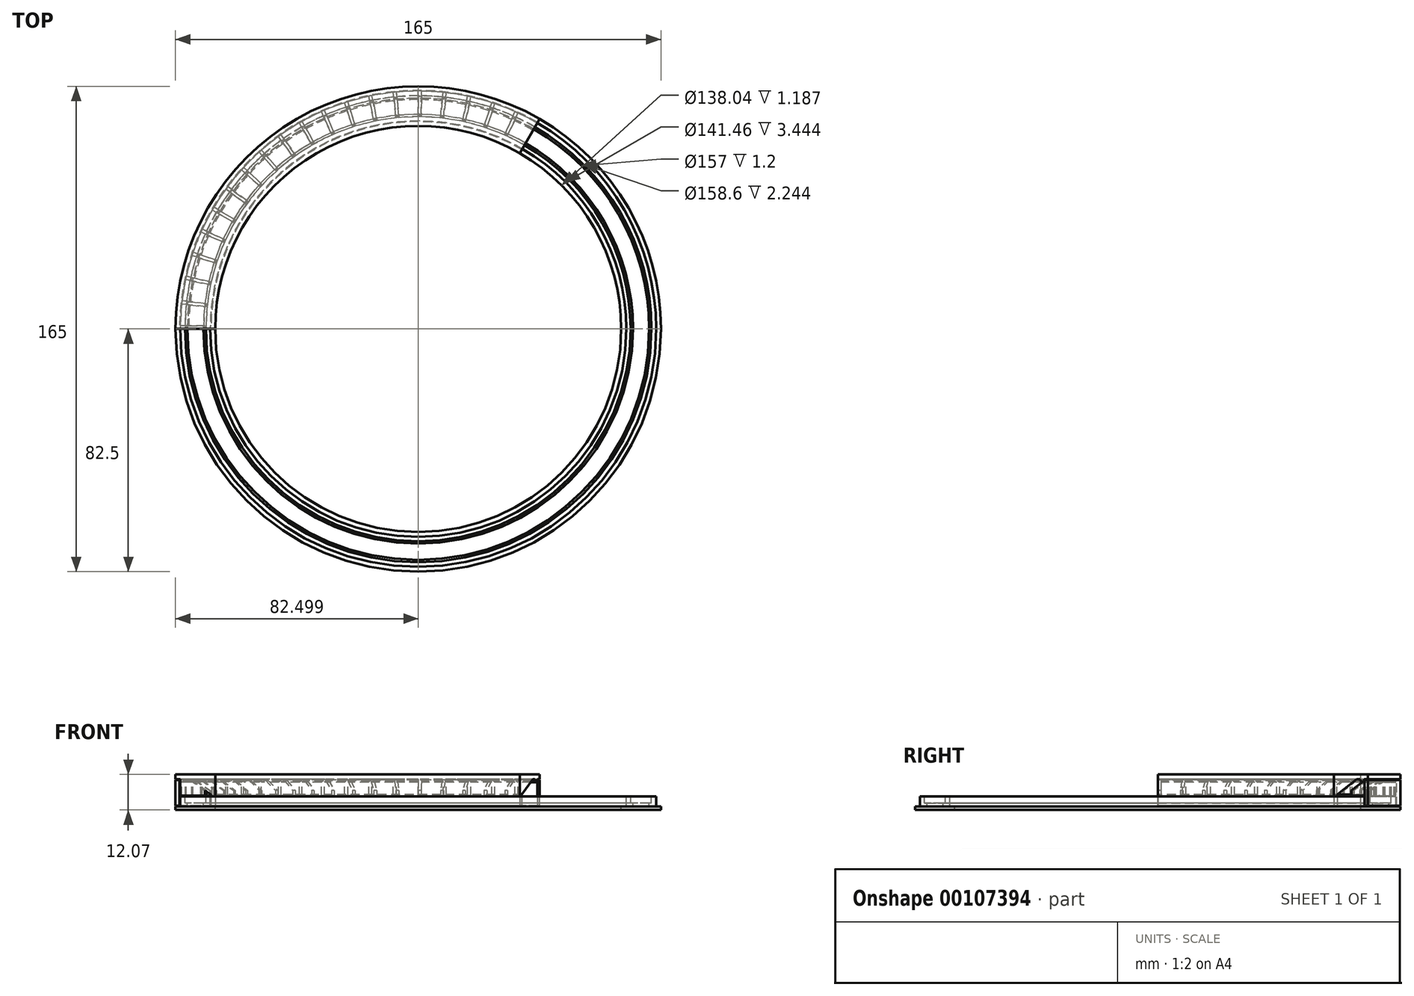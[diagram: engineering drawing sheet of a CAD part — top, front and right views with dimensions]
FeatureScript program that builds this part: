
annotation { "Feature Type Name" : "Feature", "Feature Type Description" : "" }
export const myFeature = defineFeature(function(context is Context, id is Id, definition is map)
    precondition{}
    {
        {
            var Q0;
            Q0=qCreatedBy(makeId("Front.planeOp"),FACE);
            var sketch = newSketch(context, id + "F0", { "sketchPlane" : qUnion([Q0])});
            skLineSegment(sketch, "E0", {"start": v(-1.98, -7.22) * mm, "end": v(4.52, -7.22) * mm, "construction": true});
            skLineSegment(sketch, "E1", {"start": v(-1.98, -7.22) * mm, "end": v(-1.98, -5.52) * mm, "construction": true});
            skLineSegment(sketch, "E2", {"start": v(-1.98, -5.52) * mm, "end": v(4.52, -5.52) * mm, "construction": true});
            skLineSegment(sketch, "E3", {"start": v(4.52, -5.52) * mm, "end": v(4.52, -7.22) * mm, "construction": true});
            skLineSegment(sketch, "E4", {"start": v(-0.98, -5.52) * mm, "end": v(-0.98, -3.92) * mm, "construction": true});
            skLineSegment(sketch, "E5", {"start": v(-0.98, -3.92) * mm, "end": v(3.52, -3.92) * mm, "construction": true});
            skLineSegment(sketch, "E6", {"start": v(3.52, -3.92) * mm, "end": v(3.52, -5.52) * mm, "construction": true});
            skLineSegment(sketch, "E7", {"start": v(-2.28, -8.42) * mm, "end": v(6.3, -8.42) * mm, "construction": true});
            skLineSegment(sketch, "E8", {"start": v(6.54, -4.4) * mm, "end": v(-2.28, 1.78) * mm});
            skLineSegment(sketch, "E9", {"start": v(3.52, -3.92) * mm, "end": v(3.52, -2.28) * mm, "construction": true});
            skLineSegment(sketch, "E10", {"start": v(3.52, -2.28) * mm, "end": v(-15.6, -9.24) * mm, "construction": true});
            skLineSegment(sketch, "E11", {"start": v(6.3, -8.42) * mm, "end": v(-13.34, -8.42) * mm, "construction": true});
            skLineSegment(sketch, "E12", {"start": v(8, -8.42) * mm, "end": v(6.3, -8.42) * mm});
            skLineSegment(sketch, "E13", {"start": v(-0.98, -3.92) * mm, "end": v(-0.98, 0.87) * mm, "construction": true});
            skLineSegment(sketch, "E14", {"start": v(-0.98, 0.87) * mm, "end": v(-10.79, -2.7) * mm, "construction": true});
            skLineSegment(sketch, "E15", {"start": v(-2.28, -8.42) * mm, "end": v(-3.88, -8.42) * mm});
            skLineSegment(sketch, "E16", {"start": v(-3.88, -8.42) * mm, "end": v(-3.88, -4.97) * mm});
            skLineSegment(sketch, "E17", {"start": v(-3.88, -4.97) * mm, "end": v(-2.28, -4.97) * mm});
            skLineSegment(sketch, "E18", {"start": v(-2.28, -4.97) * mm, "end": v(-2.28, -8.42) * mm});
            skLineSegment(sketch, "E19", {"start": v(-0.98, 0.87) * mm, "end": v(-3.88, 0.87) * mm});
            skLineSegment(sketch, "E20", {"start": v(-3.88, 0.87) * mm, "end": v(-3.88, 2.47) * mm});
            skLineSegment(sketch, "E21", {"start": v(-3.88, 2.47) * mm, "end": v(8, 2.47) * mm});
            skLineSegment(sketch, "E22", {"start": v(4.02, -7.22) * mm, "end": v(4.02, -8.42) * mm});
            skLineSegment(sketch, "E23", {"start": v(4.02, -8.42) * mm, "end": v(6.3, -8.42) * mm});
            skLineSegment(sketch, "E24", {"start": v(-3.88, -8.42) * mm, "end": v(-3.88, -9.6) * mm});
            skLineSegment(sketch, "E25", {"start": v(-3.88, -9.6) * mm, "end": v(6.3, -9.6) * mm});
            skLineSegment(sketch, "E26", {"start": v(6.3, -9.6) * mm, "end": v(6.3, -8.42) * mm});
            skLineSegment(sketch, "E27", {"start": v(4.02, -8.42) * mm, "end": v(-2.28, -8.42) * mm});
            skLineSegment(sketch, "E28", {"start": v(8, -8.42) * mm, "end": v(8, -9.6) * mm});
            skLineSegment(sketch, "E29", {"start": v(8, -9.6) * mm, "end": v(6.3, -9.6) * mm});
            skLineSegment(sketch, "E30", {"start": v(-2.28, -7.22) * mm, "end": v(-1.48, -7.22) * mm});
            skLineSegment(sketch, "E31", {"start": v(-1.48, -7.22) * mm, "end": v(-1.48, -8.42) * mm});
            skLineSegment(sketch, "E32", {"start": v(77.02, 5.77) * mm, "end": v(77.02, -11.17) * mm, "construction": true});
            skLineSegment(sketch, "E33", {"start": v(-3.88, -8.42) * mm, "end": v(-5.48, -8.42) * mm});
            skLineSegment(sketch, "E34", {"start": v(-5.48, -8.42) * mm, "end": v(-5.48, -9.6) * mm});
            skLineSegment(sketch, "E35", {"start": v(-5.48, -9.6) * mm, "end": v(-3.88, -9.6) * mm});
            skLineSegment(sketch, "E36", {"start": v(-2.28, 0.87) * mm, "end": v(-2.28, 0.41) * mm});
            skLineSegment(sketch, "E37", {"start": v(-3.88, -0.18) * mm, "end": v(-3.88, 0.87) * mm});
            skLineSegment(sketch, "E38", {"start": v(-3.88, 2.47) * mm, "end": v(-5.48, 2.47) * mm});
            skLineSegment(sketch, "E39", {"start": v(-5.48, 2.47) * mm, "end": v(-5.48, 0.87) * mm});
            skLineSegment(sketch, "E40", {"start": v(-5.48, 0.87) * mm, "end": v(-3.88, 0.87) * mm});
            skLineSegment(sketch, "E41", {"start": v(-5.48, 0.62) * mm, "end": v(-4.13, 0.62) * mm});
            skLineSegment(sketch, "E42", {"start": v(-4.13, 0.62) * mm, "end": v(-4.13, -8.17) * mm});
            skLineSegment(sketch, "E43", {"start": v(-4.13, -8.17) * mm, "end": v(-5.48, -8.17) * mm});
            skLineSegment(sketch, "E44", {"start": v(-5.48, -8.17) * mm, "end": v(-5.48, 0.62) * mm});
            skLineSegment(sketch, "E45", {"start": v(6.3, -5.13) * mm, "end": v(6.3, -8.42) * mm});
            skLineSegment(sketch, "E46", {"start": v(4.02, -7.22) * mm, "end": v(4.82, -7.22) * mm});
            skLineSegment(sketch, "E47", {"start": v(4.52, -4.12) * mm, "end": v(4.52, 2.47) * mm});
            skLineSegment(sketch, "E48", {"start": v(-2.28, 0.41) * mm, "end": v(-3.88, -0.18) * mm});
            skLineSegment(sketch, "E49", {"start": v(-3.88, -4.12) * mm, "end": v(-3.88, -0.18) * mm});
            skLineSegment(sketch, "E50", {"start": v(4.52, -4.12) * mm, "end": v(4.52, -4.72) * mm});
            skPoint(sketch, "E50.endSnap0", {"position": v(3.52, -4.72) * mm});
            skLineSegment(sketch, "E51", {"start": v(4.52, -4.72) * mm, "end": v(-1.98, -4.72) * mm});
            skLineSegment(sketch, "E52", {"start": v(-3.88, -4.72) * mm, "end": v(-3.88, -4.12) * mm});
            skLineSegment(sketch, "E53", {"start": v(-1.98, -4.72) * mm, "end": v(-1.98, -4.72) * mm});
            skLineSegment(sketch, "E54", {"start": v(-1.98, -4.72) * mm, "end": v(-3.88, -4.72) * mm});
            skLineSegment(sketch, "E55", {"start": v(-3.88, -4.72) * mm, "end": v(-3.88, -4.72) * mm});
            skLineSegment(sketch, "E56", {"start": v(4.82, -4.97) * mm, "end": v(4.82, -8.42) * mm});
            skLineSegment(sketch, "E57", {"start": v(4.82, -4.97) * mm, "end": v(6.3, -4.97) * mm});
            skLineSegment(sketch, "E58", {"start": v(6.3, -4.97) * mm, "end": v(6.3, -5.13) * mm});
            skLineSegment(sketch, "E59", {"start": v(4.52, -4.72) * mm, "end": v(6.54, -4.72) * mm});
            skLineSegment(sketch, "E60", {"start": v(6.54, -8.17) * mm, "end": v(8, -8.17) * mm});
            skLineSegment(sketch, "E61", {"start": v(6.54, -4.4) * mm, "end": v(6.54, -8.17) * mm});
            skLineSegment(sketch, "E62", {"start": v(8, 2.47) * mm, "end": v(8, -8.17) * mm});
            skSolve(sketch);
        }
        {
            var Q0;
            Q0=makeQuery(id+"F0.imprint","IMPRINT",FACE,{"disambiguationData":[TD([[makeQuery(id+"F0.imprint","IMPRINT",EDGE,{"derivedFrom":sQuery(id+"F0.wireOp",EDGE,"E15")}),-1.0]])]});
            var Q1;
            Q1=makeQuery(id+"F0.imprint","IMPRINT",FACE,{"disambiguationData":[TD([[makeQuery(id+"F0.imprint","IMPRINT",EDGE,{"derivedFrom":sQuery(id+"F0.wireOp",EDGE,"E15")}),1.0]])]});
            var Q2;
            {var subQ0=sQuery(id+"F0.wireOp",EDGE,"E22");Q2=makeQuery(id+"F0.imprint","IMPRINT",FACE,{"disambiguationData":[TD([[makeQuery(id+"F0.imprint","IMPRINT",EDGE,{"derivedFrom":subQ0}),1.0]])]});}
            var Q3;
            {var subQ4=sQuery(id+"F0.wireOp",EDGE,"Ndo5h7P1-a3ja-L6Ci-MCI3-Oc9OyJjJIUm8");Q3=makeQuery(id+"F0.imprint","IMPRINT",FACE,{"disambiguationData":[TD([[makeQuery(id+"F0.imprint","IMPRINT",EDGE,{"derivedFrom":subQ4}),-1.0]])]});}
            var Q4;
            {var subQ3=sQuery(id+"F0.wireOp",EDGE,"E30");Q4=makeQuery(id+"F0.imprint","IMPRINT",FACE,{"disambiguationData":[TD([[makeQuery(id+"F0.imprint","IMPRINT",EDGE,{"derivedFrom":subQ3}),-1.0]])]});}
            var Q5;
            Q5=makeQuery(id+"F0.imprint","IMPRINT",FACE,{"disambiguationData":[TD([[makeQuery(id+"F0.imprint","IMPRINT",EDGE,{"derivedFrom":sQuery(id+"F0.wireOp",EDGE,"E12")}),1.0]])]});
            var Q6;
            Q6=makeQuery(id+"F0.imprint","IMPRINT",FACE,{"disambiguationData":[TD([[makeQuery(id+"F0.imprint","IMPRINT",EDGE,{"derivedFrom":sQuery(id+"F0.wireOp",EDGE,"E24")}),-1.0]])]});
            var Q7;
            {var subQ5=sQuery(id+"F0.wireOp",EDGE,"E45");Q7=makeQuery(id+"F0.imprint","IMPRINT",FACE,{"disambiguationData":[TD([[makeQuery(id+"F0.imprint","IMPRINT",EDGE,{"derivedFrom":subQ5}),-1.0]])]});}
            var Q8;
            Q8=sQuery(id+"F0.wireOp",EDGE,"E32");
            revolve(context, id + "F1", {"entities" : qUnion([Q0, Q1, Q2, Q3, Q4, Q5, Q6, Q7]), "axis" : qUnion([Q8]), "revolveType" : RevolveType.FULL});
        }
        {
            var Q0;
            Q0=makeQuery(id+"F0.imprint","IMPRINT",FACE,{"disambiguationData":[TD([[makeQuery(id+"F0.imprint","IMPRINT",EDGE,{"derivedFrom":sQuery(id+"F0.wireOp",EDGE,"E20")}),1.0]])]});
            var Q1;
            {var subQ7=sQuery(id+"F0.wireOp",EDGE,"E12");Q1=makeQuery(id+"F0.imprint","IMPRINT",FACE,{"disambiguationData":[TD([[makeQuery(id+"F0.imprint","IMPRINT",EDGE,{"derivedFrom":subQ7}),-1.0]])]});}
            var Q2;
            {var subQ2=sQuery(id+"F0.wireOp",EDGE,"E36");Q2=makeQuery(id+"F0.imprint","IMPRINT",FACE,{"disambiguationData":[TD([[makeQuery(id+"F0.imprint","IMPRINT",EDGE,{"derivedFrom":subQ2}),-1.0]])]});}
            var Q3;
            {var subQ1=sQuery(id+"F0.wireOp",EDGE,"E20");Q3=makeQuery(id+"F0.imprint","IMPRINT",FACE,{"disambiguationData":[TD([[makeQuery(id+"F0.imprint","IMPRINT",EDGE,{"derivedFrom":subQ1}),-1.0]])]});}
            var Q4;
            {var subQ3=sQuery(id+"F0.wireOp",EDGE,"E8");var subQ7=makeQuery(id+"F0.imprint","INTERSECT",VERTEX,{"derivedFrom":[subQ3,sQuery(id+"F0.wireOp",EDGE,"E19")]});Q4=makeQuery(id+"F0.imprint","IMPRINT",FACE,{"disambiguationData":[TD([[makeQuery(id+"F0.imprint","IMPRINT",EDGE,{"disambiguationData":[TD([[subQ7,1.0]])],"derivedFrom":subQ3}),-1.0]])]});}
            var Q5;
            {var subQ0=sQuery(id+"F0.wireOp",EDGE,"E19");var subQ1=sQuery(id+"F0.wireOp",EDGE,"E8");var subQ2=makeQuery(id+"F0.imprint","INTERSECT",VERTEX,{"derivedFrom":[subQ1,subQ0]});Q5=makeQuery(id+"F0.imprint","IMPRINT",FACE,{"disambiguationData":[TD([[makeQuery(id+"F0.imprint","IMPRINT",EDGE,{"disambiguationData":[TD([[subQ2,-1.0]])],"derivedFrom":subQ1}),1.0]])]});}
            var Q6;
            {var subQ5=sQuery(id+"F0.wireOp",EDGE,"E60");Q6=makeQuery(id+"F0.imprint","IMPRINT",FACE,{"disambiguationData":[TD([[makeQuery(id+"F0.imprint","IMPRINT",EDGE,{"derivedFrom":subQ5}),1.0]])]});}
            var Q7;
            Q7=sQuery(id+"F0.wireOp",EDGE,"E32");
            revolve(context, id + "F2", {"entities" : qUnion([Q0, Q1, Q2, Q3, Q4, Q5, Q6]), "axis" : qUnion([Q7]), "revolveType" : RevolveType.ONE_DIRECTION, "angle" : 120 * degree});
        }
        {
            var Q0;
            Q0=makeQuery(id+"F0.imprint","IMPRINT",FACE,{"disambiguationData":[TD([[makeQuery(id+"F0.imprint","IMPRINT",EDGE,{"derivedFrom":sQuery(id+"F0.wireOp",EDGE,"E41")}),-1.0]])]});
            var Q1;
            Q1=sQuery(id+"F0.wireOp",EDGE,"E32");
            revolve(context, id + "F3", {"entities" : qUnion([Q0]), "axis" : qUnion([Q1]), "revolveType" : RevolveType.ONE_DIRECTION, "angle" : 120 * degree});
        }
        {
            var Q0;
            {var subQ6=sQuery(id+"F0.wireOp",EDGE,"E36");Q0=makeQuery(id+"F0.imprint","IMPRINT",FACE,{"disambiguationData":[TD([[makeQuery(id+"F0.imprint","IMPRINT",EDGE,{"derivedFrom":subQ6}),1.0]])]});}
            var Q1;
            {var subQ2=sQuery(id+"F0.wireOp",EDGE,"E36");Q1=makeQuery(id+"F0.imprint","IMPRINT",FACE,{"disambiguationData":[TD([[makeQuery(id+"F0.imprint","IMPRINT",EDGE,{"derivedFrom":subQ2}),-1.0]])]});}
            var Q2;
            {var subQ0=sQuery(id+"F0.wireOp",EDGE,"E20");Q2=makeQuery(id+"F0.imprint","IMPRINT",FACE,{"disambiguationData":[TD([[makeQuery(id+"F0.imprint","IMPRINT",EDGE,{"derivedFrom":subQ0}),-1.0]])]});}
            var Q3;
            Q3=sQuery(id+"F0.wireOp",EDGE,"E32");
            revolve(context, id + "F4", {"entities" : qUnion([Q0, Q1, Q2]), "axis" : qUnion([Q3]), "revolveType" : RevolveType.ONE_DIRECTION, "angle" : 0.8 * degree});
        }
        {
            var Q0;
            Q0=makeQuery(id+"F4.opRevolve","SWEPT_BODY",BODY,{"disambiguationData":[OSD([sQuery(id+"F0.wireOp",EDGE,"E21"),sQuery(id+"F0.wireOp",EDGE,"MbaugKXz-nLJl-PvIg-yBW8-Y2HkV5LabatY"),sQuery(id+"F0.wireOp",EDGE,"E47"),sQuery(id+"F0.wireOp",EDGE,"2ttpRtf7-95J1-ebSC-xGsn-WReD2H8fU9RS")])]});
            var Q1;
            Q1=sQuery(id+"F0.wireOp",EDGE,"E32");
            circularPattern(context, id + "F5", {"operationType" : NewBodyOperationType.ADD, "entities" : qUnion([Q0]), "axis" : qUnion([Q1]), "angle" : 6 * degree, "instanceCount" : 20});
        }
    });
